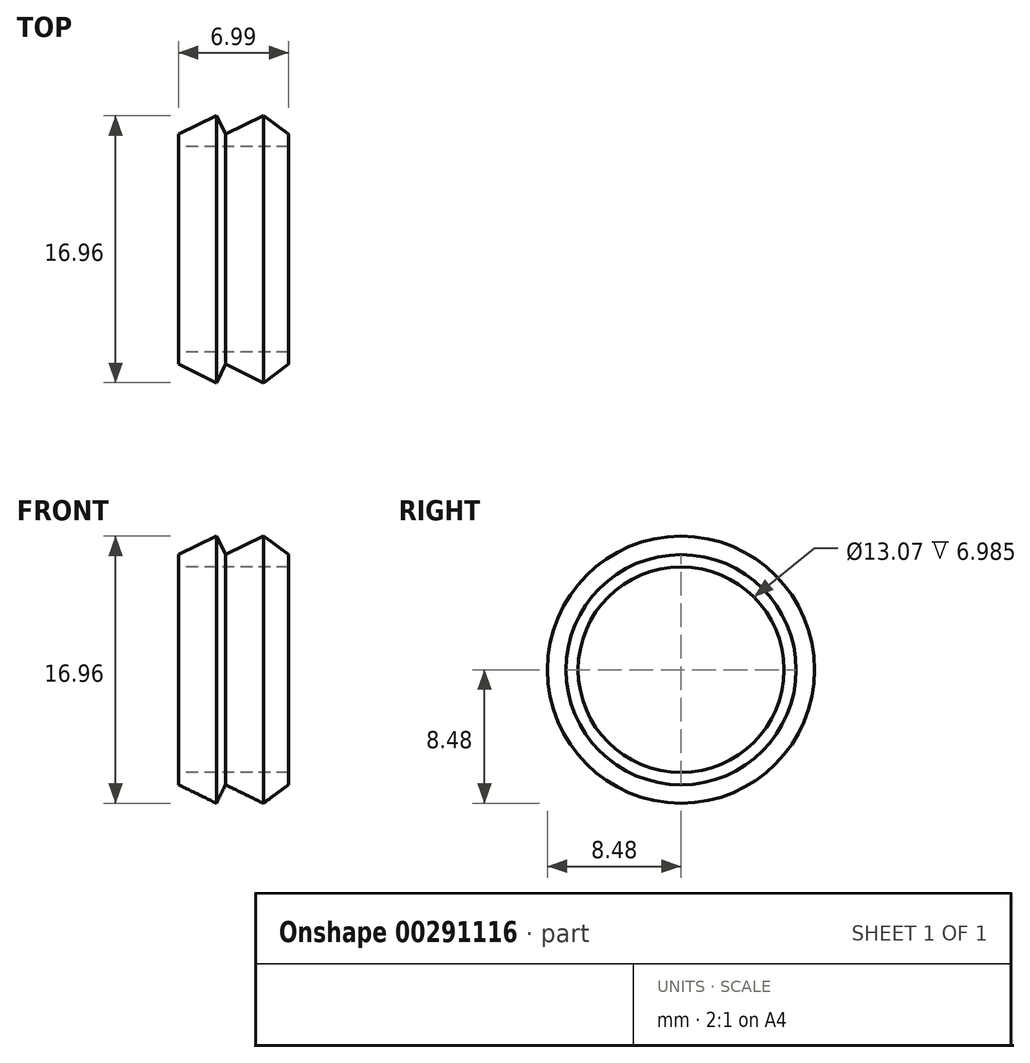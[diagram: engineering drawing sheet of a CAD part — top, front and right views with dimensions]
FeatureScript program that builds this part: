
annotation { "Feature Type Name" : "Feature", "Feature Type Description" : "" }
export const myFeature = defineFeature(function(context is Context, id is Id, definition is map)
    precondition{}
    {
        {
            var Q0;
            Q0=qCreatedBy(makeId("Front.planeOp"),FACE);
            var sketch = newSketch(context, id + "F0", { "sketchPlane" : qUnion([Q0])});
            skLineSegment(sketch, "E0", {"start": v(0, 0) * mm, "end": v(6.99, 0) * mm});
            skLineSegment(sketch, "E1", {"start": v(0, 0) * mm, "end": v(0, 7.3) * mm});
            skLineSegment(sketch, "E2", {"start": v(0, 7.3) * mm, "end": v(6.99, 7.3) * mm});
            skLineSegment(sketch, "E3", {"start": v(6.99, 7.3) * mm, "end": v(6.99, 0) * mm});
            skLineSegment(sketch, "E4", {"start": v(0, 0) * mm, "end": v(-12.76, 0) * mm});
            skLineSegment(sketch, "E5", {"start": v(0, 7.3) * mm, "end": v(2.4, 8.48) * mm});
            skLineSegment(sketch, "E6", {"start": v(2.4, 8.48) * mm, "end": v(2.98, 7.3) * mm});
            skLineSegment(sketch, "E7", {"start": v(2.98, 7.3) * mm, "end": v(5.38, 8.48) * mm});
            skLineSegment(sketch, "E8", {"start": v(5.38, 8.48) * mm, "end": v(6.99, 7.3) * mm});
            skLineSegment(sketch, "E9.MirrorCS", {"start": v(0, -7.3) * mm, "end": v(2.4, -8.48) * mm});
            skLineSegment(sketch, "E10.MirrorCS", {"start": v(2.4, -8.48) * mm, "end": v(2.98, -7.3) * mm});
            skLineSegment(sketch, "E11.MirrorCS", {"start": v(2.98, -7.3) * mm, "end": v(5.38, -8.48) * mm});
            skLineSegment(sketch, "E12.MirrorCS", {"start": v(5.38, -8.48) * mm, "end": v(6.99, -7.3) * mm});
            skSolve(sketch);
        }
        {
            var Q0;
            Q0=makeQuery(id+"F0.imprint","IMPRINT",FACE,{"disambiguationData":[TD([[makeQuery(id+"F0.imprint","IMPRINT",EDGE,{"derivedFrom":sQuery(id+"F0.wireOp",EDGE,"E0")}),1.0]])]});
            var Q1;
            {var subQ0=sQuery(id+"F0.wireOp",EDGE,"E5");Q1=makeQuery(id+"F0.imprint","IMPRINT",FACE,{"disambiguationData":[TD([[makeQuery(id+"F0.imprint","IMPRINT",EDGE,{"derivedFrom":subQ0}),-1.0]])]});}
            var Q2;
            {var subQ2=sQuery(id+"F0.wireOp",EDGE,"E7");Q2=makeQuery(id+"F0.imprint","IMPRINT",FACE,{"disambiguationData":[TD([[makeQuery(id+"F0.imprint","IMPRINT",EDGE,{"derivedFrom":subQ2}),-1.0]])]});}
            var Q3;
            Q3=sQuery(id+"F0.wireOp",EDGE,"E4");
            revolve(context, id + "F1", {"entities" : qUnion([Q0, Q1, Q2]), "axis" : qUnion([Q3]), "revolveType" : RevolveType.FULL});
        }
        {
            var Q0;
            Q0=makeQuery(id+"F1.opRevolve","SWEPT_FACE",FACE,{"disambiguationData":[OSD([sQuery(id+"F0.wireOp",EDGE,"E1")])]});
            var sketch = newSketch(context, id + "F2", { "sketchPlane" : qUnion([Q0])});
            skCircle(sketch, "E13", {"center": v(0, 0) * mm, "radius": 6.53 * mm});
            skSolve(sketch);
        }
        {
            var Q0;
            Q0 = qSketchRegion(id + "F2", true);
            extrude(context, id + "F3", {"entities" : qUnion([Q0]), "operationType" : NewBodyOperationType.REMOVE, "oppositeDirection" : true, "depth" : 25.4 * mm});
        }
    });
